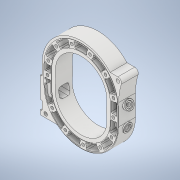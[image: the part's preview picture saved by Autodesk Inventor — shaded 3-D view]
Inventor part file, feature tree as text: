
AUTODESK INVENTOR PART (.ipt)
format: ipt  version: 2021 (Build 250183000, 183)  size: 636,416 bytes
history: native  units: in
note: dims shown in document units (in); Inventor stores cm internally (conversion verified against a paired STEP export)
features: thread x4, other x2, extrude x1, sketch x1
ambient origin geometry x8: Origin, YZ Plane, XZ Plane, XY Plane, X Axis, Y Axis, Z Axis, Center Point
bodies: Solid2 (feature_tree), Solid1 (feature_tree)
feature tree (8):
  thread  "Thread1"  [1 undecoded]
  thread  "Thread2"  [1 undecoded]
  thread  "Thread3"  [1 undecoded]
  thread  "Thread4"  [1 undecoded]
  extrude  "Extrusion1"  Depth=141.7323in TaperAngle=0.0deg
  sketch  "Sketch1"  dims[d8=0.0in d9=141.7323in d10=0.0in d11=141.7323in d12=3.3268in d13=0.4843in d14=0.0in d15=0.0in]
  other  "2D Equation Curve1"
  other  "2D Equation Curve2"
note: 4 required parameter values undecoded (feature->parameter linkage not recoverable at this tier; creation-order binding heuristic only, values carry confidence <= 0.55)
